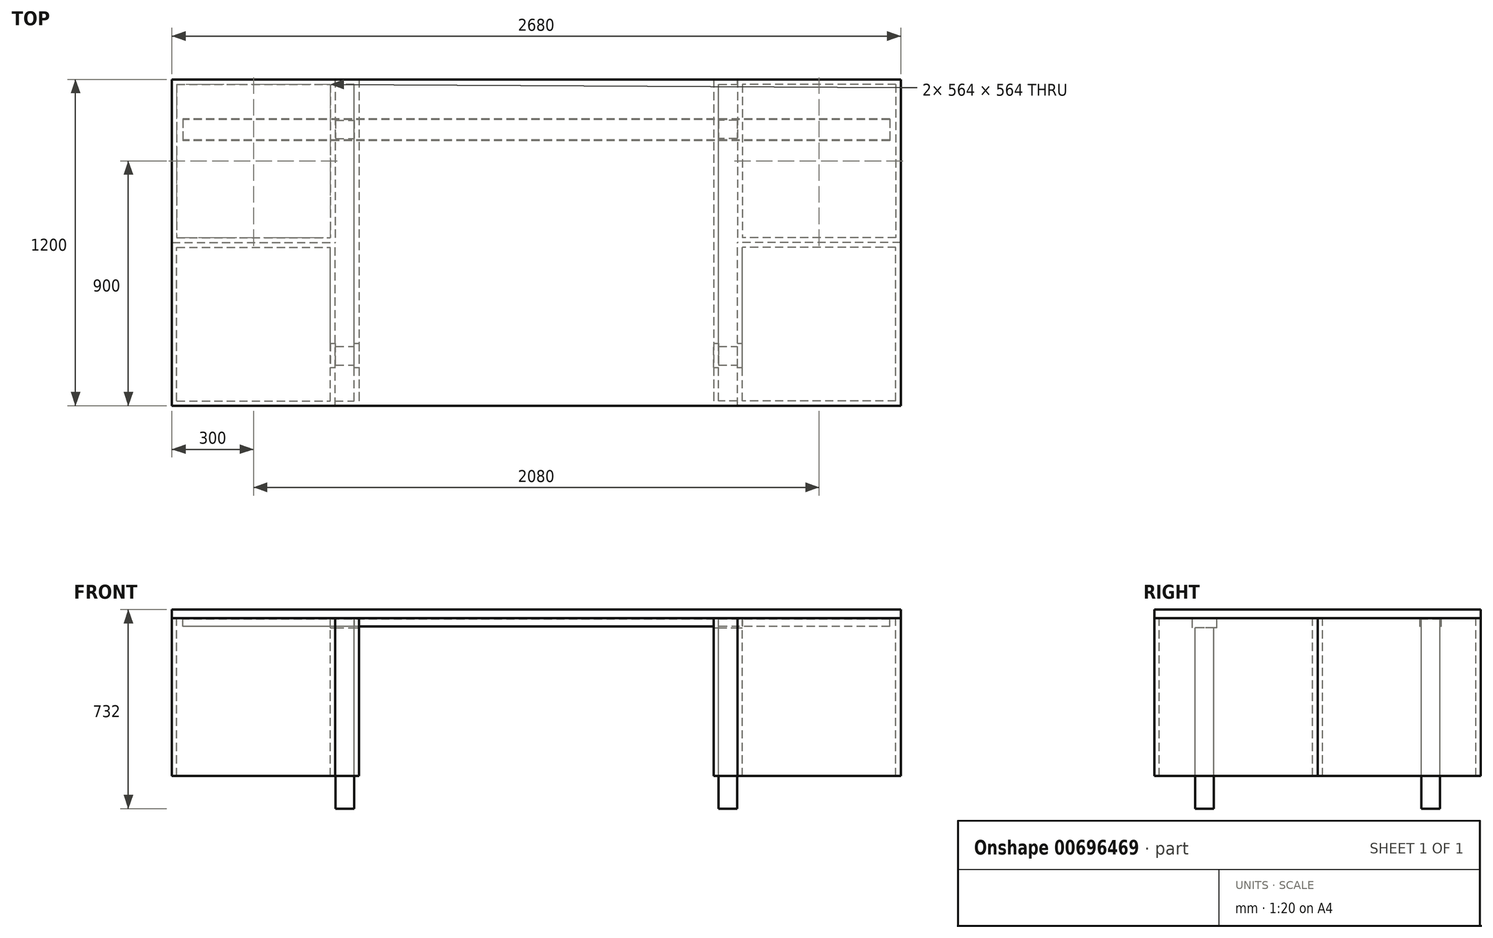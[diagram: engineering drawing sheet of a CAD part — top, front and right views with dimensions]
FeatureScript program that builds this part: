
annotation { "Feature Type Name" : "Feature", "Feature Type Description" : "" }
export const myFeature = defineFeature(function(context is Context, id is Id, definition is map)
    precondition{}
    {
        {
            var Q0;
            Q0=qCreatedBy(makeId("Top.planeOp"),FACE);
            var sketch = newSketch(context, id + "F0", { "sketchPlane" : qUnion([Q0])});
            skLineSegment(sketch, "E0.bottom", {"start": v(-1340, 600) * mm, "end": v(1340, 600) * mm});
            skLineSegment(sketch, "E0.top", {"start": v(-1340, -600) * mm, "end": v(1340, -600) * mm});
            skLineSegment(sketch, "E0.left", {"start": v(-1340, 600) * mm, "end": v(-1340, -600) * mm});
            skLineSegment(sketch, "E0.right", {"start": v(1340, 600) * mm, "end": v(1340, -600) * mm});
            skPoint(sketch, "E0.middle", {"position": v(0, 0) * mm});
            skSolve(sketch);
        }
        {
            var Q0;
            Q0=makeQuery(id+"F0.imprint","IMPRINT",FACE,{"disambiguationData":[TD([[makeQuery(id+"F0.imprint","IMPRINT",EDGE,{"derivedFrom":sQuery(id+"F0.wireOp",EDGE,"E0.bottom")}),-1.0]])]});
            extrude(context, id + "F1", {"entities" : qUnion([Q0]), "depth" : 32 * mm, "offsetDistance" : 25 * mm});
        }
        {
            var Q0;
            Q0=makeQuery(id+"F1.opExtrude","CAP_FACE",FACE,{"disambiguationData":[OSD([sQuery(id+"F0.wireOp",EDGE,"E0.bottom"),sQuery(id+"F0.wireOp",EDGE,"E0.top"),sQuery(id+"F0.wireOp",EDGE,"E0.left"),sQuery(id+"F0.wireOp",EDGE,"E0.right")])],"isStart":true});
            var sketch = newSketch(context, id + "F2", { "sketchPlane" : qUnion([Q0])});
            skLineSegment(sketch, "E1.bottom", {"start": v(-1340, -600) * mm, "end": v(-740, -600) * mm});
            skLineSegment(sketch, "E1.top", {"start": v(-1340, 0) * mm, "end": v(-740, 0) * mm});
            skLineSegment(sketch, "E1.left", {"start": v(-1340, -600) * mm, "end": v(-1340, 0) * mm});
            skLineSegment(sketch, "E1.right", {"start": v(-740, -600) * mm, "end": v(-740, 0) * mm});
            skLineSegment(sketch, "E2.0", {"start": v(-1322, -18) * mm, "end": v(-758, -18) * mm});
            skLineSegment(sketch, "E2.1", {"start": v(-1322, -582) * mm, "end": v(-1322, -18) * mm});
            skLineSegment(sketch, "E2.2", {"start": v(-1322, -582) * mm, "end": v(-758, -582) * mm});
            skLineSegment(sketch, "E2.3", {"start": v(-758, -582) * mm, "end": v(-758, -18) * mm});
            skSolve(sketch);
        }
        {
            var Q0;
            Q0=makeQuery(id+"F2.imprint","IMPRINT",FACE,{"disambiguationData":[TD([[makeQuery(id+"F2.imprint","IMPRINT",EDGE,{"derivedFrom":sQuery(id+"F2.wireOp",EDGE,"E1.bottom")}),1.0]])]});
            extrude(context, id + "F3", {"entities" : qUnion([Q0]), "depth" : 580 * mm, "offsetDistance" : 25 * mm});
        }
        {
            var Q0;
            Q0=makeQuery(id+"F3.opExtrude","SWEPT_BODY",BODY,{"disambiguationData":[OSD([sQuery(id+"F2.wireOp",EDGE,"E1.bottom"),sQuery(id+"F2.wireOp",EDGE,"E1.top"),sQuery(id+"F2.wireOp",EDGE,"E1.left"),sQuery(id+"F2.wireOp",EDGE,"E1.right"),sQuery(id+"F2.wireOp",EDGE,"E2.0"),sQuery(id+"F2.wireOp",EDGE,"E2.1"),sQuery(id+"F2.wireOp",EDGE,"E2.2"),sQuery(id+"F2.wireOp",EDGE,"E2.3")])]});
            var Q1;
            Q1=makeQuery(id+"F3.opExtrude","SWEPT_FACE",FACE,{"disambiguationData":[OSD([sQuery(id+"F2.wireOp",EDGE,"E1.top")])]});
            mirror(context, id + "F4", {"entities" : qUnion([Q0]), "mirrorPlane" : qUnion([Q1])});
        }
        {
            var Q0;
            Q0=makeQuery(id+"F4.opPattern","COPY",BODY,{"derivedFrom":makeQuery(id+"F3.opExtrude","SWEPT_BODY",BODY,{"disambiguationData":[OSD([sQuery(id+"F2.wireOp",EDGE,"E1.bottom"),sQuery(id+"F2.wireOp",EDGE,"E1.top"),sQuery(id+"F2.wireOp",EDGE,"E1.left"),sQuery(id+"F2.wireOp",EDGE,"E1.right"),sQuery(id+"F2.wireOp",EDGE,"E2.0"),sQuery(id+"F2.wireOp",EDGE,"E2.1"),sQuery(id+"F2.wireOp",EDGE,"E2.2"),sQuery(id+"F2.wireOp",EDGE,"E2.3")])]}),"instanceName":"1"});
            var Q1;
            Q1=makeQuery(id+"F3.opExtrude","SWEPT_BODY",BODY,{"disambiguationData":[OSD([sQuery(id+"F2.wireOp",EDGE,"E1.bottom"),sQuery(id+"F2.wireOp",EDGE,"E1.top"),sQuery(id+"F2.wireOp",EDGE,"E1.left"),sQuery(id+"F2.wireOp",EDGE,"E1.right"),sQuery(id+"F2.wireOp",EDGE,"E2.0"),sQuery(id+"F2.wireOp",EDGE,"E2.1"),sQuery(id+"F2.wireOp",EDGE,"E2.2"),sQuery(id+"F2.wireOp",EDGE,"E2.3")])]});
            var Q2;
            Q2=qCreatedBy(makeId("Right.planeOp"),FACE);
            mirror(context, id + "F5", {"entities" : qUnion([Q0, Q1]), "mirrorPlane" : qUnion([Q2])});
        }
        {
            var Q0;
            Q0=makeQuery(id+"F1.opExtrude","CAP_FACE",FACE,{"disambiguationData":[OSD([sQuery(id+"F0.wireOp",EDGE,"E0.bottom"),sQuery(id+"F0.wireOp",EDGE,"E0.top"),sQuery(id+"F0.wireOp",EDGE,"E0.left"),sQuery(id+"F0.wireOp",EDGE,"E0.right")])],"isStart":true});
            var sketch = newSketch(context, id + "F6", { "sketchPlane" : qUnion([Q0])});
            skLineSegment(sketch, "E3", {"start": v(-740, 582) * mm, "end": v(-670, 582) * mm});
            skLineSegment(sketch, "E4", {"start": v(-670, 582) * mm, "end": v(-670, -582) * mm});
            skLineSegment(sketch, "E5", {"start": v(-670, -582) * mm, "end": v(-740, -582) * mm});
            skLineSegment(sketch, "E6", {"start": v(-740, -582) * mm, "end": v(-740, -600) * mm});
            skLineSegment(sketch, "E7", {"start": v(-740, -600) * mm, "end": v(-652, -600) * mm});
            skLineSegment(sketch, "E8", {"start": v(-652, -600) * mm, "end": v(-652, 600) * mm});
            skLineSegment(sketch, "E9", {"start": v(-652, 600) * mm, "end": v(-740, 600) * mm});
            skLineSegment(sketch, "E10", {"start": v(-740, 600) * mm, "end": v(-740, 582) * mm});
            skLineSegment(sketch, "E11.bottom", {"start": v(-738, 450) * mm, "end": v(-670, 450) * mm});
            skLineSegment(sketch, "E11.top", {"start": v(-738, 382) * mm, "end": v(-670, 382) * mm});
            skLineSegment(sketch, "E11.left", {"start": v(-738, 450) * mm, "end": v(-738, 382) * mm});
            skLineSegment(sketch, "E11.right", {"start": v(-670, 450) * mm, "end": v(-670, 382) * mm});
            skSolve(sketch);
        }
        {
            var Q0;
            Q0=makeQuery(id+"F6.imprint","IMPRINT",FACE,{"disambiguationData":[TD([[makeQuery(id+"F6.imprint","IMPRINT",EDGE,{"derivedFrom":sQuery(id+"F6.wireOp",EDGE,"E3")}),1.0]])]});
            var Q1;
            Q1=makeQuery(id+"F4.opPattern","COPY",FACE,{"derivedFrom":makeQuery(id+"F3.opExtrude","CAP_FACE",FACE,{"disambiguationData":[OSD([sQuery(id+"F2.wireOp",EDGE,"E1.bottom"),sQuery(id+"F2.wireOp",EDGE,"E1.top"),sQuery(id+"F2.wireOp",EDGE,"E1.left"),sQuery(id+"F2.wireOp",EDGE,"E1.right"),sQuery(id+"F2.wireOp",EDGE,"E2.0"),sQuery(id+"F2.wireOp",EDGE,"E2.1"),sQuery(id+"F2.wireOp",EDGE,"E2.2"),sQuery(id+"F2.wireOp",EDGE,"E2.3")])],"isStart":false}),"instanceName":"1"});
            extrude(context, id + "F7", {"entities" : qUnion([Q0]), "endBound" : BoundingType.UP_TO_SURFACE, "depth" : 25 * mm, "endBoundEntityFace" : qUnion([Q1]), "offsetDistance" : 25 * mm});
        }
        {
            var Q0;
            Q0=makeQuery(id+"F7.opExtrude","SWEPT_BODY",BODY,{"disambiguationData":[OSD([sQuery(id+"F6.wireOp",EDGE,"E3"),sQuery(id+"F6.wireOp",EDGE,"E4"),sQuery(id+"F6.wireOp",EDGE,"E5"),sQuery(id+"F6.wireOp",EDGE,"E6"),sQuery(id+"F6.wireOp",EDGE,"E7"),sQuery(id+"F6.wireOp",EDGE,"E8"),sQuery(id+"F6.wireOp",EDGE,"E9"),sQuery(id+"F6.wireOp",EDGE,"E10")])]});
            var Q1;
            Q1=qCreatedBy(makeId("Right.planeOp"),FACE);
            mirror(context, id + "F8", {"entities" : qUnion([Q0]), "mirrorPlane" : qUnion([Q1])});
        }
        {
            var Q0;
            Q0=makeQuery(id+"F6.imprint","IMPRINT",FACE,{"disambiguationData":[TD([[makeQuery(id+"F6.imprint","IMPRINT",EDGE,{"derivedFrom":sQuery(id+"F6.wireOp",EDGE,"E11.bottom")}),-1.0]])]});
            var Q1;
            Q1=makeQuery(id+"F7.opExtrude","CAP_FACE",FACE,{"disambiguationData":[OSD([sQuery(id+"F2.wireOp",EDGE,"E1.bottom"),sQuery(id+"F2.wireOp",EDGE,"E1.top"),sQuery(id+"F2.wireOp",EDGE,"E1.left"),sQuery(id+"F2.wireOp",EDGE,"E1.right"),sQuery(id+"F2.wireOp",EDGE,"E2.0"),sQuery(id+"F2.wireOp",EDGE,"E2.1"),sQuery(id+"F2.wireOp",EDGE,"E2.2"),sQuery(id+"F2.wireOp",EDGE,"E2.3")])],"isStart":false});
            extrude(context, id + "F9", {"entities" : qUnion([Q0]), "depth" : 700 * mm, "endBoundEntityFace" : qUnion([Q1]), "offsetDistance" : 25 * mm});
        }
        {
            var Q0;
            Q0=makeQuery(id+"F9.opExtrude","SWEPT_BODY",BODY,{"disambiguationData":[OSD([sQuery(id+"F6.wireOp",EDGE,"E11.bottom"),sQuery(id+"F6.wireOp",EDGE,"E11.top"),sQuery(id+"F6.wireOp",EDGE,"E11.left"),sQuery(id+"F6.wireOp",EDGE,"E11.right")])]});
            var Q1;
            Q1=qCreatedBy(makeId("Front.planeOp"),FACE);
            mirror(context, id + "F10", {"entities" : qUnion([Q0]), "mirrorPlane" : qUnion([Q1])});
        }
        {
            var Q0;
            Q0=makeQuery(id+"F9.opExtrude","SWEPT_BODY",BODY,{"disambiguationData":[OSD([sQuery(id+"F6.wireOp",EDGE,"E11.bottom"),sQuery(id+"F6.wireOp",EDGE,"E11.top"),sQuery(id+"F6.wireOp",EDGE,"E11.left"),sQuery(id+"F6.wireOp",EDGE,"E11.right")])]});
            var Q1;
            Q1=makeQuery(id+"F10.opPattern","COPY",BODY,{"derivedFrom":makeQuery(id+"F9.opExtrude","SWEPT_BODY",BODY,{"disambiguationData":[OSD([sQuery(id+"F6.wireOp",EDGE,"E11.bottom"),sQuery(id+"F6.wireOp",EDGE,"E11.top"),sQuery(id+"F6.wireOp",EDGE,"E11.left"),sQuery(id+"F6.wireOp",EDGE,"E11.right")])]}),"instanceName":"1"});
            var Q2;
            Q2=qCreatedBy(makeId("Right.planeOp"),FACE);
            mirror(context, id + "F11", {"entities" : qUnion([Q0, Q1]), "mirrorPlane" : qUnion([Q2])});
        }
        {
            var Q0;
            Q0=qCreatedBy(makeId("Right.planeOp"),FACE);
            var sketch = newSketch(context, id + "F12", { "sketchPlane" : qUnion([Q0])});
            skLineSegment(sketch, "E12", {"start": v(-455, -30) * mm, "end": v(-455, 0) * mm});
            skLineSegment(sketch, "E13", {"start": v(-455, 0) * mm, "end": v(-375, 0) * mm});
            skLineSegment(sketch, "E14", {"start": v(-375, 0) * mm, "end": v(-375, -30) * mm});
            skLineSegment(sketch, "E15", {"start": v(-455, -30) * mm, "end": v(-452, -30) * mm});
            skLineSegment(sketch, "E16", {"start": v(-452, -30) * mm, "end": v(-452, -3) * mm});
            skLineSegment(sketch, "E17", {"start": v(-452, -3) * mm, "end": v(-378, -3) * mm});
            skLineSegment(sketch, "E18", {"start": v(-378, -3) * mm, "end": v(-378, -30) * mm});
            skLineSegment(sketch, "E19", {"start": v(-378, -30) * mm, "end": v(-375, -30) * mm});
            skLineSegment(sketch, "E20.bottom", {"start": v(-460, 0) * mm, "end": v(-370, 0) * mm});
            skLineSegment(sketch, "E20.top", {"start": v(-460, -35) * mm, "end": v(-370, -35) * mm});
            skLineSegment(sketch, "E20.left", {"start": v(-460, 0) * mm, "end": v(-460, -35) * mm});
            skLineSegment(sketch, "E20.right", {"start": v(-370, 0) * mm, "end": v(-370, -35) * mm});
            skSolve(sketch);
        }
        {
            var Q0;
            {var subQ1=sQuery(id+"F12.wireOp",EDGE,"E12");Q0=makeQuery(id+"F12.imprint","IMPRINT",FACE,{"disambiguationData":[TD([[makeQuery(id+"F12.imprint","IMPRINT",EDGE,{"derivedFrom":subQ1}),-1.0]])]});}
            var Q1;
            Q1=makeQuery(id+"F5.opPattern","COPY",FACE,{"derivedFrom":makeQuery(id+"F4.opPattern","COPY",FACE,{"derivedFrom":makeQuery(id+"F3.opExtrude","SWEPT_FACE",FACE,{"disambiguationData":[OSD([sQuery(id+"F2.wireOp",EDGE,"E2.1")])]}),"instanceName":"1"}),"instanceName":"1"});
            extrude(context, id + "F13", {"entities" : qUnion([Q0]), "endBound" : BoundingType.SYMMETRIC, "depth" : 2600 * mm, "endBoundEntityFace" : qUnion([Q1]), "offsetDistance" : 25 * mm});
        }
        {
            var Q0;
            Q0=makeQuery(id+"F13.opExtrude","SWEPT_BODY",BODY,{"disambiguationData":[OSD([sQuery(id+"F12.wireOp",EDGE,"E12"),sQuery(id+"F12.wireOp",EDGE,"E14"),sQuery(id+"F12.wireOp",EDGE,"E15"),sQuery(id+"F12.wireOp",EDGE,"E16"),sQuery(id+"F12.wireOp",EDGE,"E17"),sQuery(id+"F12.wireOp",EDGE,"E18"),sQuery(id+"F12.wireOp",EDGE,"E19"),sQuery(id+"F12.wireOp",EDGE,"E20.bottom")])]});
            var Q1;
            Q1=qCreatedBy(makeId("Front.planeOp"),FACE);
            mirror(context, id + "F14", {"entities" : qUnion([Q0]), "mirrorPlane" : qUnion([Q1])});
        }
        {
            var Q0;
            Q0 = qSketchRegion(id + "F12", true);
            extrude(context, id + "F15", {"entities" : qUnion([Q0]), "operationType" : NewBodyOperationType.REMOVE, "endBound" : BoundingType.SYMMETRIC, "oppositeDirection" : true, "depth" : 2600 * mm, "offsetDistance" : 25 * mm});
        }
    });
